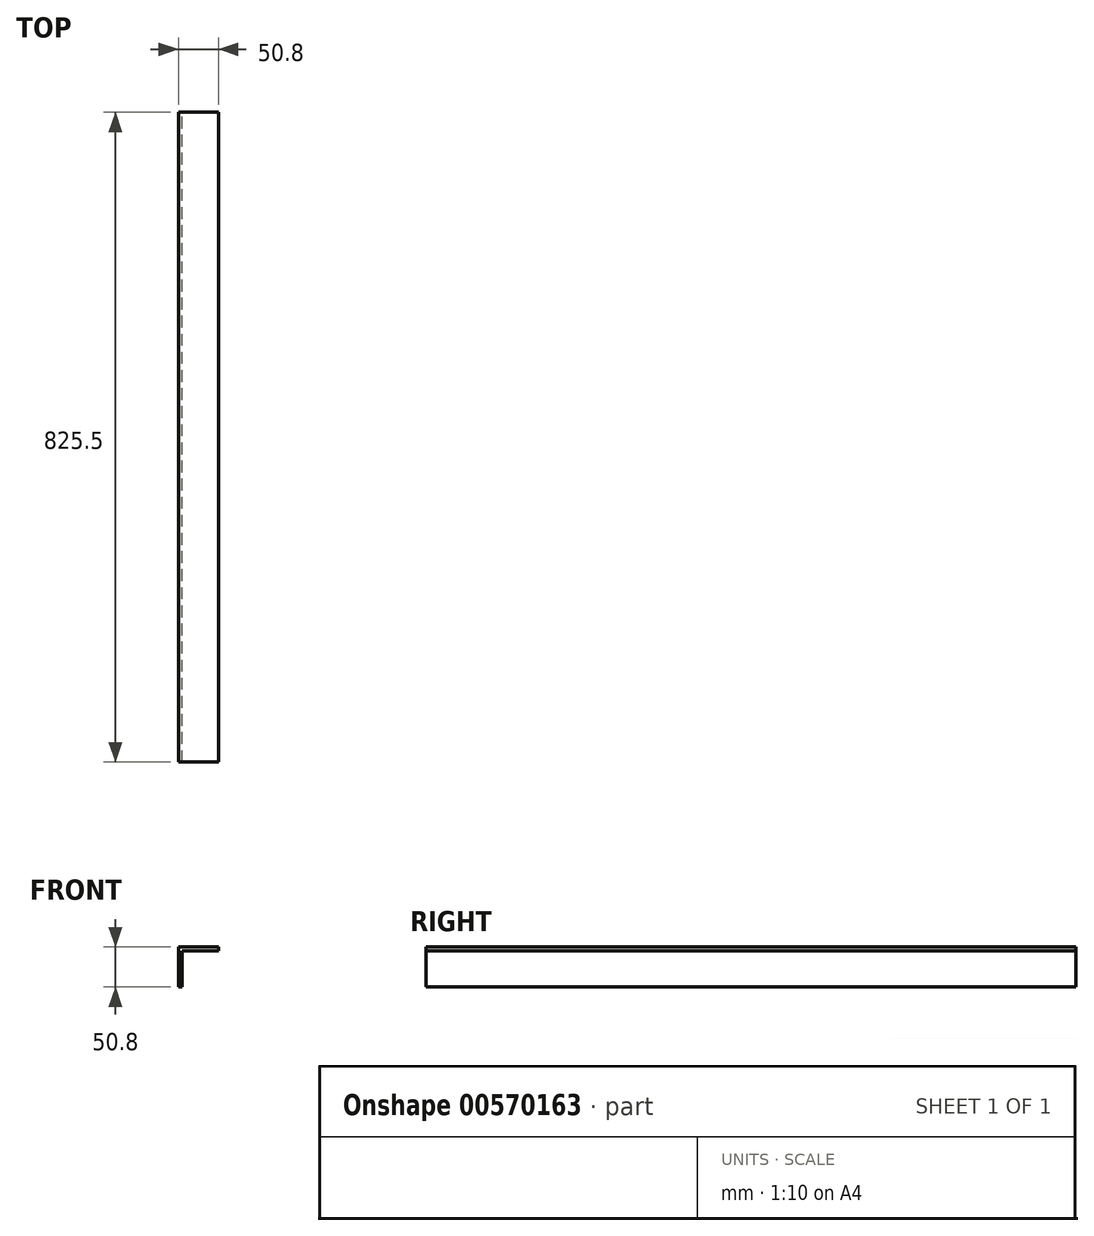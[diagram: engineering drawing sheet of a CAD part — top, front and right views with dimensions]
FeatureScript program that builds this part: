
annotation { "Feature Type Name" : "Feature", "Feature Type Description" : "" }
export const myFeature = defineFeature(function(context is Context, id is Id, definition is map)
    precondition{}
    {
        {
            var Q0;
            Q0=qCreatedBy(makeId("Front.planeOp"),FACE);
            var sketch = newSketch(context, id + "F0", { "sketchPlane" : qUnion([Q0])});
            skLineSegment(sketch, "E0", {"start": v(0, 0) * mm, "end": v(0, 50.8) * mm});
            skLineSegment(sketch, "E1", {"start": v(0, 50.8) * mm, "end": v(50.8, 50.8) * mm});
            skLineSegment(sketch, "E2", {"start": v(50.8, 50.8) * mm, "end": v(50.8, 46.04) * mm});
            skLineSegment(sketch, "E3", {"start": v(50.8, 46.04) * mm, "end": v(4.76, 46.04) * mm});
            skLineSegment(sketch, "E4", {"start": v(4.76, 46.04) * mm, "end": v(4.76, 0) * mm});
            skLineSegment(sketch, "E5", {"start": v(4.76, 0) * mm, "end": v(0, 0) * mm});
            skSolve(sketch);
        }
        {
            var Q0;
            Q0=makeQuery(id+"F0.imprint","IMPRINT",FACE,{"disambiguationData":[TD([[makeQuery(id+"F0.imprint","IMPRINT",EDGE,{"derivedFrom":sQuery(id+"F0.wireOp",EDGE,"E0")}),-1.0]])]});
            extrude(context, id + "F1", {"entities" : qUnion([Q0]), "depth" : 825.5 * mm, "offsetDistance" : 25.4 * mm});
        }
    });
